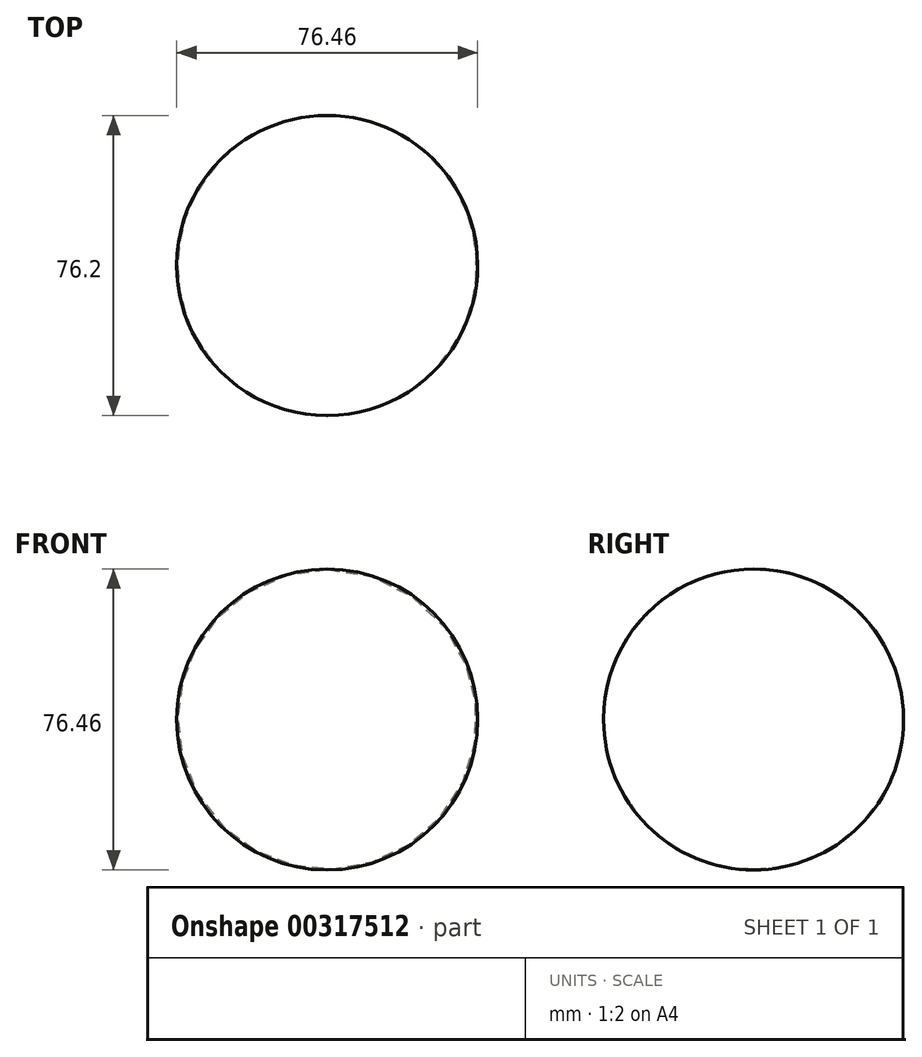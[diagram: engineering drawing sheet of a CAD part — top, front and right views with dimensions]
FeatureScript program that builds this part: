
annotation { "Feature Type Name" : "Feature", "Feature Type Description" : "" }
export const myFeature = defineFeature(function(context is Context, id is Id, definition is map)
    precondition{}
    {
        {
            var Q0;
            Q0=qCreatedBy(makeId("Top.planeOp"),FACE);
            var sketch = newSketch(context, id + "F0", { "sketchPlane" : qUnion([Q0])});
            skLineSegment(sketch, "E0", {"start": v(0, -36.89) * mm, "end": v(0, 39.31) * mm});
            skArc(sketch, "E1", {"start": v(0, -36.89) * mm, "mid": v(38.23, 1.21) * mm, "end": v(0, 39.31) * mm});
            skSolve(sketch);
        }
        {
            var Q0;
            Q0 = qSketchRegion(id + "F0", true);
            var Q1;
            Q1=sQuery(id+"F0.wireOp",EDGE,"E0");
            revolve(context, id + "F1", {"entities" : qUnion([Q0]), "axis" : qUnion([Q1]), "revolveType" : RevolveType.FULL});
        }
    });
